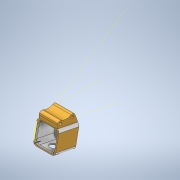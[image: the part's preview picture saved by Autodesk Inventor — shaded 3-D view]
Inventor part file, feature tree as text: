
AUTODESK INVENTOR PART (.ipt)
format: ipt  version: 2020 (Build 240168000, 168)  size: 244,224 bytes
history: native  units: mm
features: other x3, sketch x3, extrude x1, projected_geometry x1
ambient origin geometry x8: Origin, YZ Plane, XZ Plane, XY Plane, X Axis, Y Axis, Z Axis, Center Point
bodies: Solid2 (feature_tree)
feature tree (8):
  other  "V2 modular session template.iam"
  other  "V2 modular session camera case.ipt:1"
  other  "V2 modular session frame mount.ipt:1"
  extrude  "Extrusion1"  Depth=10.0mm TaperAngle=0.0deg
  sketch  "Sketch6"  dims[d1=10.0mm d2=10.0mm d3=0.0mm]
  sketch  "Sketch7"
  sketch  "Sketch8"
  projected_geometry  "Projected Loop1"
